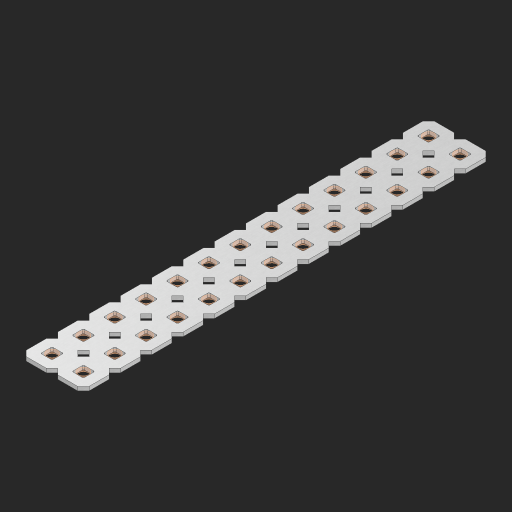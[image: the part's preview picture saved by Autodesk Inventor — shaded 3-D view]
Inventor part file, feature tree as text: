
AUTODESK INVENTOR PART (.ipt)
format: ipt  version: 2023 (Build 270158000, 158)  size: 570,368 bytes
history: native  units: in
note: dims shown in document units (in); Inventor stores cm internally (conversion verified against a paired STEP export)
features: other x27, extrude x25, sketch x2, pattern_linear x1
ambient origin geometry x8: Origin, YZ Plane, XZ Plane, XY Plane, X Axis, Y Axis, Z Axis, Center Point
bodies: Solid1 (feature_tree), Body (feature_tree)
feature tree (55):
  pattern_linear  "Rectangular Pattern1"  Spacing1=0.09in  [1 undecoded]
  sketch  "Sketch1"  dims[d1=0.5in]
  sketch  "Sketch2"  dims[d2=0.182in d3=0.09in d4=0.09in d5=0.09in d6=0.09in d7=0.09in d8=0.09in d9=0.09in d10=0.09in d11=0.02in d13=0.0in d14=0.172in d15=0.0625in d16=0.0in d19=0.5in d22=0.5in]
  other  "Srf1"
  other  "Srf126"
  other  "Srf127"
  other  "Srf128"
  other  "Srf129"
  other  "Srf130"
  other  "Srf131"
  other  "Srf250"
  other  "Srf251"
  other  "Srf252"
  other  "Srf253"
  other  "Srf254"
  other  "Srf255"
  other  "Srf268"
  other  "Srf269"
  other  "Srf270"
  other  "Srf271"
  other  "Srf272"
  other  "Srf273"
  other  "Srf274"
  other  "Srf275"
  other  "Srf276"
  other  "Srf277"
  other  "Srf278"
  other  "Srf279"
  other  "Srf280"
  other  "Circle"
  extrude  "ExtrusionSrf126"  Depth=0.09in
  extrude  "ExtrusionSrf127"  Depth=0.09in
  extrude  "ExtrusionSrf128"  Depth=0.09in
  extrude  "ExtrusionSrf129"  Depth=0.09in
  extrude  "ExtrusionSrf130"  Depth=0.09in
  extrude  "ExtrusionSrf131"  Depth=0.09in
  extrude  "ExtrusionSrf250"  Depth=0.09in
  extrude  "ExtrusionSrf251"  Depth=0.02in
  extrude  "ExtrusionSrf252"  TaperAngle=0.0deg  [1 undecoded]
  extrude  "ExtrusionSrf253"  Depth=0.5in
  extrude  "ExtrusionSrf254"  Depth=0.0625in TaperAngle=0.0deg
  extrude  "ExtrusionSrf255"  Depth=0.5in
  extrude  "ExtrusionSrf268"  Depth=0.5in
  extrude  "ExtrusionSrf269"  [1 undecoded]
  extrude  "ExtrusionSrf270"  [1 undecoded]
  extrude  "ExtrusionSrf271"  [1 undecoded]
  extrude  "ExtrusionSrf272"  [1 undecoded]
  extrude  "ExtrusionSrf273"  [1 undecoded]
  extrude  "ExtrusionSrf274"  [1 undecoded]
  extrude  "ExtrusionSrf275"  [1 undecoded]
  extrude  "ExtrusionSrf276"  [1 undecoded]
  extrude  "ExtrusionSrf277"  [1 undecoded]
  extrude  "ExtrusionSrf278"  [1 undecoded]
  extrude  "ExtrusionSrf279"  [1 undecoded]
  extrude  "ExtrusionSrf280"  [1 undecoded]
note: 14 required parameter values undecoded (feature->parameter linkage not recoverable at this tier; creation-order binding heuristic only, values carry confidence <= 0.55)
